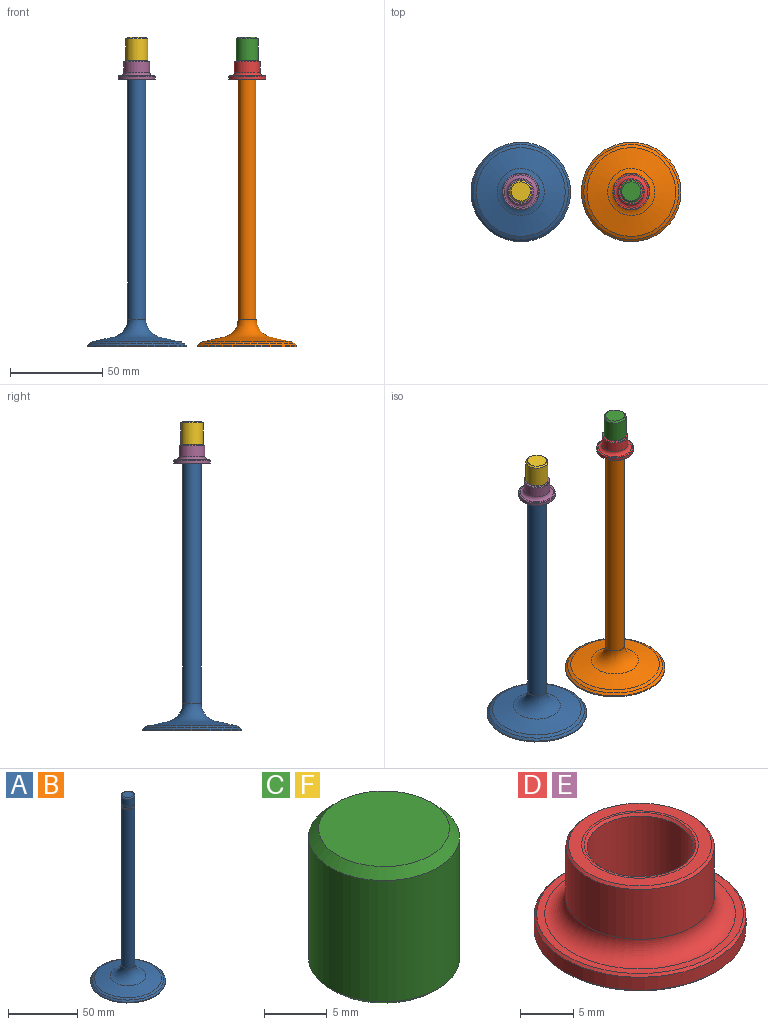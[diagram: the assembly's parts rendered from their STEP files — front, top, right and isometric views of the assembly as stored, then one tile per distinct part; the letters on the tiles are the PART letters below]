
ASSEMBLY  parts=6 mates=3
PART A: 13 faces, bbox 54x54x165 mm
  f0: plane 54x54mm, normal (0,0,-1), area 2290.2mm2, adj f8
  f1: plane 8x8mm, normal (0,0,1), area 50.3mm2, adj f12
  f2: cylinder r=5mm len=10mm, axis (0,0,-1), area 188.5mm2, adj f3,f12
  f3: plane 10x10mm, normal (0,0,-1), area 28.3mm2, adj f2,f4
  f4: cylinder r=4mm len=8mm, axis (0,0,-1), area 75.4mm2, adj f3,f5
  f5: plane 10x10mm, normal (0,0,1), area 28.3mm2, adj f4,f6
  f6: cylinder r=5mm len=140.02mm, axis (0,0,-1), area 4398.8mm2, adj f5,f9
  f7: cone r=5mm half-angle=77.2deg, axis (0,0,-1), area 1340.7mm2, adj f9,f11
  f8: cylinder r=27mm len=54mm, axis (0,0,-1), area 108.1mm2, adj f0,f10
  f9: torus R=15mm, axis (0,0,-1), area 657.1mm2, adj f6,f7
  f10: cone r=27mm half-angle=47.2deg, axis (0,0,-1), area 275mm2, adj f8,f11
  f11: cone r=24.07mm half-angle=62.2deg, axis (0,0,-1), area 302.6mm2, adj f7,f10
  f12: torus R=4mm, axis (0,0,-1), area 45.8mm2, adj f1,f2
PART B: same geometry as A
PART C: 8 faces, bbox 12x12x13 mm
  f0: cylinder r=6mm len=12mm, axis (0,0,-1), area 444.8mm2, adj f5,f7
  f1: plane 10.4x10.4mm, normal (0,0,1), area 84.9mm2, adj f5
  f2: plane 11.2x11.2mm, normal (0,0,-1), area 6.9mm2, adj f6,f7
  f3: cylinder r=5mm len=10mm, axis (0,0,-1), area 301.6mm2, adj f4,f6
  f4: plane 10x10mm, normal (0,0,-1), area 78.5mm2, adj f3
  f5: cone r=5.2mm half-angle=45deg, axis (0,0,-1), area 39.8mm2, adj f0,f1
  f6: cone r=5mm half-angle=45deg, axis (0,0,-1), area 18.5mm2, adj f2,f3
  f7: cone r=6mm half-angle=45deg, axis (0,0,1), area 20.6mm2, adj f0,f2
PART D: 13 faces, bbox 22.6x22.6x10 mm
  f0: plane 13.5x13.5mm, normal (0,0,1), area 48.1mm2, adj f5,f11
  f1: plane 19.5x19.5mm, normal (0,0,1), area 44.2mm2, adj f7,f12
  f2: cylinder r=10mm len=20mm, axis (0,0,-1), area 94.2mm2, adj f7,f10
  f3: plane 19.5x19.5mm, normal (0,0,-1), area 212.1mm2, adj f8,f10
  f4: cylinder r=7mm len=14mm, axis (0,0,-1), area 252.9mm2, adj f11,f12
  f5: plane 11x11mm, normal (0,0,1), area 8.4mm2, adj f0,f9
  f6: cylinder r=5mm len=10mm, axis (0,0,1), area 298.5mm2, adj f8,f9
  f7: cone r=9.75mm half-angle=45deg, axis (0,0,-1), area 21.9mm2, adj f1,f2
  f8: cone r=5.25mm half-angle=45deg, axis (0,0,-1), area 11.4mm2, adj f3,f6
  f9: cone r=5mm half-angle=45deg, axis (0,0,1), area 11.4mm2, adj f5,f6
  f10: cone r=10mm half-angle=45deg, axis (0,0,1), area 21.9mm2, adj f2,f3
  f11: cone r=6.75mm half-angle=45deg, axis (0,0,-1), area 15.3mm2, adj f0,f4
  f12: torus R=9mm, axis (0,0,1), area 152.5mm2, adj f1,f4
PART E: same geometry as D
PART F: same geometry as C
PLACE A t=(-60,0,0)mm
PLACE B at identity fixed
PLACE C t=(0,0,155)mm
PLACE D t=(0,0,145)mm
PLACE E t=(-60,0,145)mm
PLACE F t=(-60,0,155)mm
MATE fastened F.f0 <-> E.f2  axis (0,0,-1) through (-60,0,155)mm
MATE fastened A.f2 <-> B.f0  axis (0,0,-1) through (-60,0,0)mm
MATE fastened D.f2 <-> C.f0  axis (0,0,1) through (0,0,155)mm
